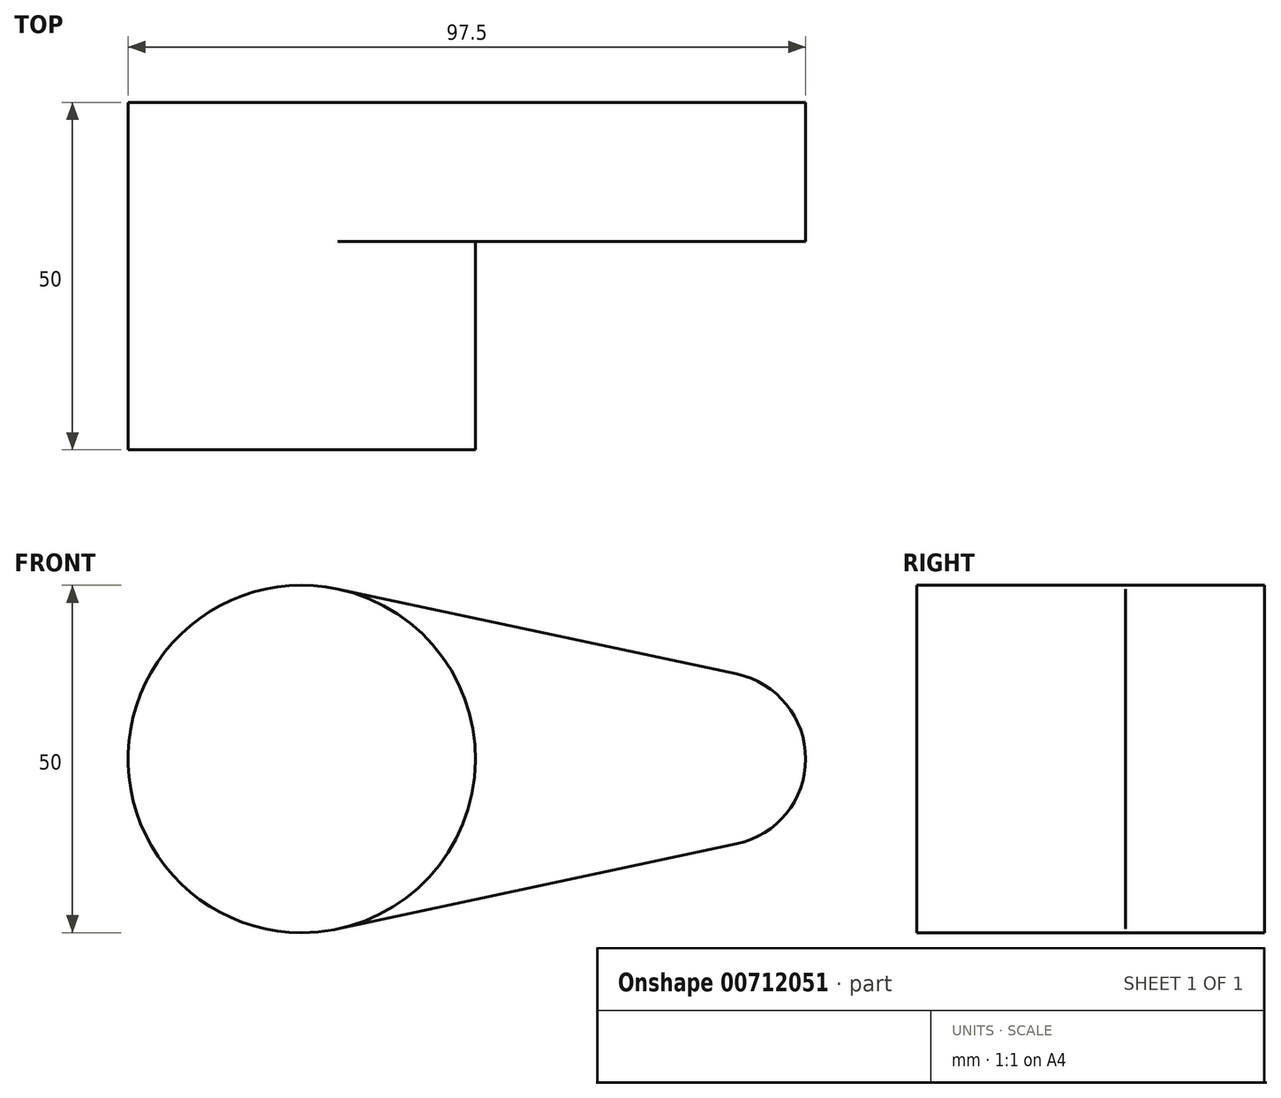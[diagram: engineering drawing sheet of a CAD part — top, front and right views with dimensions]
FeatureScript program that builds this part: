
annotation { "Feature Type Name" : "Feature", "Feature Type Description" : "" }
export const myFeature = defineFeature(function(context is Context, id is Id, definition is map)
    precondition{}
    {
        {
            var Q0;
            Q0=qCreatedBy(makeId("Front.planeOp"),FACE);
            var sketch = newSketch(context, id + "F0", { "sketchPlane" : qUnion([Q0])});
            skCircle(sketch, "E0", {"center": v(0, 0) * mm, "radius": 25 * mm});
            skCircle(sketch, "E1", {"center": v(60, 0) * mm, "radius": 12.5 * mm});
            skLineSegment(sketch, "E2", {"start": v(5.2, 24.45) * mm, "end": v(62.6, 12.23) * mm});
            skLineSegment(sketch, "E3", {"start": v(5.2, -24.45) * mm, "end": v(62.6, -12.23) * mm});
            skSolve(sketch);
        }
        {
            var Q0;
            Q0 = qSketchRegion(id + "F0", true);
            extrude(context, id + "F1", {"entities" : qUnion([Q0]), "depth" : 20 * mm, "offsetDistance" : 25 * mm});
        }
        {
            var Q0;
            {var subQ0=sQuery(id+"F0.wireOp",EDGE,"E0");var subQ1=makeQuery(id+"F0.imprint","INTERSECT",VERTEX,{"derivedFrom":[subQ0,sQuery(id+"F0.wireOp",EDGE,"E2")]});Q0=makeQuery(id+"F0.imprint","IMPRINT",FACE,{"disambiguationData":[TD([[makeQuery(id+"F0.imprint","IMPRINT",EDGE,{"disambiguationData":[TD([[subQ1,-1.0]])],"derivedFrom":subQ0}),1.0]])]});}
            extrude(context, id + "F2", {"entities" : qUnion([Q0]), "operationType" : NewBodyOperationType.ADD, "depth" : 50 * mm, "offsetDistance" : 25 * mm});
        }
    });
